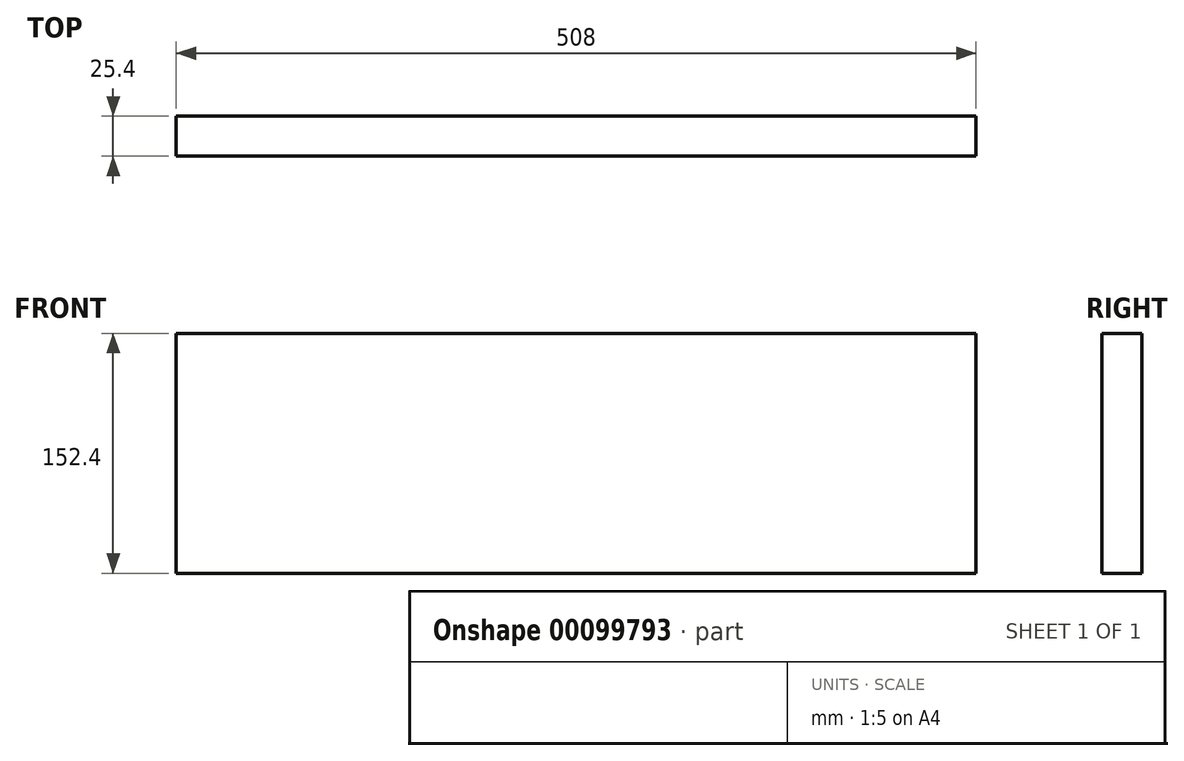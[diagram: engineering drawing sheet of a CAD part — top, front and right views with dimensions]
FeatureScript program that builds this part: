
annotation { "Feature Type Name" : "Feature", "Feature Type Description" : "" }
export const myFeature = defineFeature(function(context is Context, id is Id, definition is map)
    precondition{}
    {
        {
            var Q0;
            Q0=qCreatedBy(makeId("Front.planeOp"),FACE);
            var sketch = newSketch(context, id + "F0", { "sketchPlane" : qUnion([Q0])});
            skLineSegment(sketch, "E0", {"start": v(-260.02, -58.28) * mm, "end": v(247.98, -58.28) * mm});
            skLineSegment(sketch, "E1", {"start": v(-260.02, -58.28) * mm, "end": v(-260.02, 94.12) * mm});
            skLineSegment(sketch, "E2", {"start": v(247.98, -58.28) * mm, "end": v(247.98, 94.12) * mm});
            skLineSegment(sketch, "E3", {"start": v(-260.02, 94.12) * mm, "end": v(247.98, 94.12) * mm});
            skSolve(sketch);
        }
        {
            var Q0;
            Q0=makeQuery(id+"F0.imprint","IMPRINT",FACE,{"disambiguationData":[TD([[makeQuery(id+"F0.imprint","IMPRINT",EDGE,{"derivedFrom":sQuery(id+"F0.wireOp",EDGE,"E0")}),1.0]])]});
            extrude(context, id + "F1", {"entities" : qUnion([Q0]), "depth" : 25.4 * mm});
        }
    });
